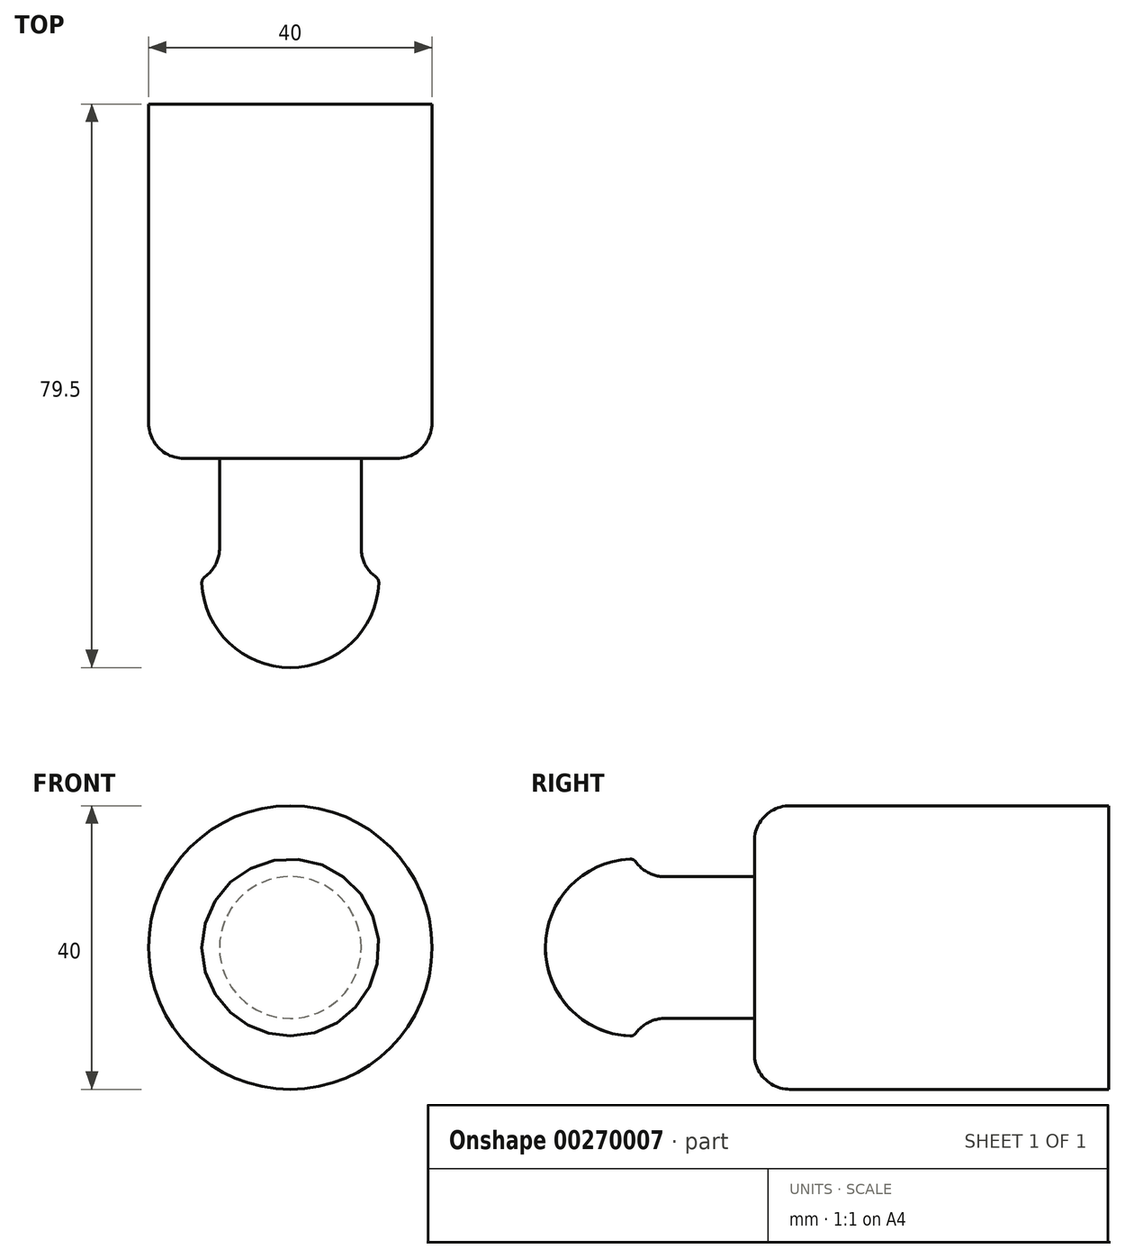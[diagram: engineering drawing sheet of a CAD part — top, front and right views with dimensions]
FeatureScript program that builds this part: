
annotation { "Feature Type Name" : "Feature", "Feature Type Description" : "" }
export const myFeature = defineFeature(function(context is Context, id is Id, definition is map)
    precondition{}
    {
        {
            var Q0;
            Q0=qCreatedBy(makeId("Front.planeOp"),FACE);
            var sketch = newSketch(context, id + "F0", { "sketchPlane" : qUnion([Q0])});
            skCircle(sketch, "E0", {"center": v(0, 0) * mm, "radius": 20 * mm});
            skSolve(sketch);
        }
        {
            var Q0;
            Q0=makeQuery(id+"F0.imprint","IMPRINT",FACE,{"disambiguationData":[TD([[makeQuery(id+"F0.imprint","IMPRINT",EDGE,{"derivedFrom":sQuery(id+"F0.wireOp",EDGE,"E0")}),1.0]])]});
            extrude(context, id + "F1", {"entities" : qUnion([Q0]), "depth" : 50 * mm});
        }
        {
            var Q0;
            Q0=makeQuery(id+"F1.opExtrude","CAP_FACE",FACE,{"disambiguationData":[OSD([sQuery(id+"F0.wireOp",EDGE,"E0")])],"isStart":false});
            var sketch = newSketch(context, id + "F2", { "sketchPlane" : qUnion([Q0])});
            skCircle(sketch, "E1", {"center": v(0, 0) * mm, "radius": 10 * mm});
            skSolve(sketch);
        }
        {
            var Q0;
            Q0=makeQuery(id+"F2.imprint","IMPRINT",FACE,{"disambiguationData":[TD([[makeQuery(id+"F2.imprint","IMPRINT",EDGE,{"derivedFrom":sQuery(id+"F2.wireOp",EDGE,"E1")}),1.0]])]});
            extrude(context, id + "F3", {"entities" : qUnion([Q0]), "operationType" : NewBodyOperationType.ADD, "depth" : 20 * mm});
        }
        {
            var Q0;
            Q0=makeQuery(id+"F3.opExtrude","CAP_EDGE",EDGE,{"disambiguationData":[OSD([sQuery(id+"F2.wireOp",EDGE,"E1")])],"isStart":true});
            var Q1;
            Q1=makeQuery(id+"F1.opExtrude","CAP_EDGE",EDGE,{"disambiguationData":[OSD([sQuery(id+"F0.wireOp",EDGE,"E0")])],"isStart":false});
            fillet(context, id + "F4", {"entities" : qUnion([Q0, Q1]), "radius" : 5 * mm, "tangentPropagation" : true, "allowEdgeOverflow" : false});
        }
        {
            var Q0;
            Q0=makeQuery(id+"F3.opExtrude","CAP_FACE",FACE,{"disambiguationData":[OSD([sQuery(id+"F2.wireOp",EDGE,"E1")])],"isStart":false});
            cPlane(context, id + "F5", {"entities" : qUnion([Q0]), "cplaneType" : CPlaneType.OFFSET, "offset" : 3 * mm, "oppositeDirection" : true, "width" : 150 * mm, "height" : 150 * mm});
        }
        {
            var Q0;
            Q0=qCreatedBy(id+"F5.planeOp",FACE);
            var sketch = newSketch(context, id + "F6", { "sketchPlane" : qUnion([Q0])});
            skCircle(sketch, "E2", {"center": v(0, 0) * mm, "radius": 12.5 * mm});
            skSolve(sketch);
        }
        {
            var Q0;
            Q0=makeQuery(id+"F6.imprint","IMPRINT",FACE,{"disambiguationData":[TD([[makeQuery(id+"F6.imprint","IMPRINT",EDGE,{"derivedFrom":sQuery(id+"F6.wireOp",EDGE,"E2")}),1.0]])]});
            extrude(context, id + "F7", {"entities" : qUnion([Q0]), "operationType" : NewBodyOperationType.ADD, "depth" : 12.5 * mm});
        }
        {
            var Q0;
            Q0=makeQuery(id+"F7.opExtrude","CAP_FACE",FACE,{"disambiguationData":[OSD([sQuery(id+"F6.wireOp",EDGE,"E2")])],"isStart":false});
            fillet(context, id + "F8", {"entities" : qUnion([Q0]), "radius" : 12.5 * mm, "tangentPropagation" : true, "allowEdgeOverflow" : false});
        }
        {
            var Q0;
            Q0=makeQuery(id+"F7.boolean.opBoolean","INTERSECT",EDGE,{"derivedFrom":[makeQuery(id+"F3.opExtrude","SWEPT_FACE",FACE,{"disambiguationData":[OSD([sQuery(id+"F2.wireOp",EDGE,"E1")])]}),makeQuery(id+"F7.opExtrude","CAP_FACE",FACE,{"disambiguationData":[OSD([sQuery(id+"F6.wireOp",EDGE,"E2")])],"isStart":true})]});
            fillet(context, id + "F9", {"entities" : qUnion([Q0]), "radius" : 5 * mm, "tangentPropagation" : true, "allowEdgeOverflow" : false});
        }
        {
            var Q0;
            {var subQ0=sQuery(id+"F6.wireOp",EDGE,"E2");Q0=makeQuery(id+"F9.opFillet","BLEND_EDGE",EDGE,{"blendedFrom":[makeQuery(id+"F7.boolean.opBoolean","INTERSECT",EDGE,{"derivedFrom":[makeQuery(id+"F3.opExtrude","SWEPT_FACE",FACE,{"disambiguationData":[OSD([sQuery(id+"F2.wireOp",EDGE,"E1")])]}),makeQuery(id+"F7.opExtrude","CAP_FACE",FACE,{"disambiguationData":[OSD([subQ0])],"isStart":true})]}),makeQuery(id+"F8.opFillet","BLEND_FACE",FACE,{"disambiguationData":[OSD([subQ0])]})],"blendedInto":[makeQuery(id+"F8.opFillet","BLEND_FACE",FACE,{"disambiguationData":[OSD([subQ0])]})]});}
            fillet(context, id + "F10", {"entities" : qUnion([Q0]), "radius" : 1 * mm, "tangentPropagation" : true, "allowEdgeOverflow" : false});
        }
    });
